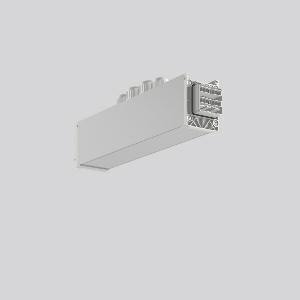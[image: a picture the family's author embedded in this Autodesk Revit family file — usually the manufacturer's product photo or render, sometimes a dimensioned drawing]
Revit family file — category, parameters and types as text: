
# Revit family: linedo_mitteleinspeisung_7pol_s_s_982698_000_5_89da
name_source: partatom
category: Lighting Fixtures
units: mm (PartAtom-declared; Revit-internal decimal feet)

## family parameters
Cut with Voids When Loaded = No
Host = Face
Light Source = No
Part Type = Normal
Room Calculation Point = No
Round Connector Dimension = Use Diameter
Shared = No

## types (1)
- LINEDO_Mitteleinspeisung_7pol_S_S
    Apparent Load = 0 VA
    Default Elevation = 1800 mm
    Description = Series: LINEDO
Middle power feed, 7-pole, connection plug / plug. Housing: extruded aluminium profile, anodised. Cover made of plastic, surface like housing. LINEDO plug system, plastic, light grey. 4 cable glands (2 x M20 and 2 x M25). Cable glands on top. Easy connection for rigid or flexible wires.
Colour: anodised aluminium
Length: 349 mm
Width: 58 mm
Height: 76 mm
Weight: 751 g
    Height = 76 mm
    Lamp = 0 x
    Length = 349 mm
    Luminous efficacy = 0 lm/W
    Manufacturer = RZB
    ModVariant = No
    Model = 982698.000.5
    Mounting Place = Ceiling
    Mounting Type = Surface mounted, Pendant
    Number of Poles = 1
    OnlyDefault = Yes
    Power Factor = 1
    Product Name = LINEDO_Mitteleinspeisung_7pol_S_S
    Product group = Surface mounted continuous line luminaire system
    ProductGroupID = 310
    Protection Class = Protection class I
    Protection Degree = IP 54
    RLX_Detail_Level = 1
    RLX_Emergency_Light_Flux = 0 lm
    RLX_Emergency_Type = 0
    RLX_Emergency_Type_DB = No
    RlxData = <blob elided: 21837 chars, md5=02e21962>
    Standby Power = 0 W
    System Light Flux = 0 lm
    System Power = 0 W
    Type Comments = Product without accessories
    Type Image = 982698.000.2.jpg
    URL = http://relux.com
    VarID = ---
    Voltage = 0 V
    Weight = 0.00 kg
    Width = 58 mm

## geometry (parser evidence)
native form markers: Blend x4, Sweep x10
no freeform markers — native parametric forms only
